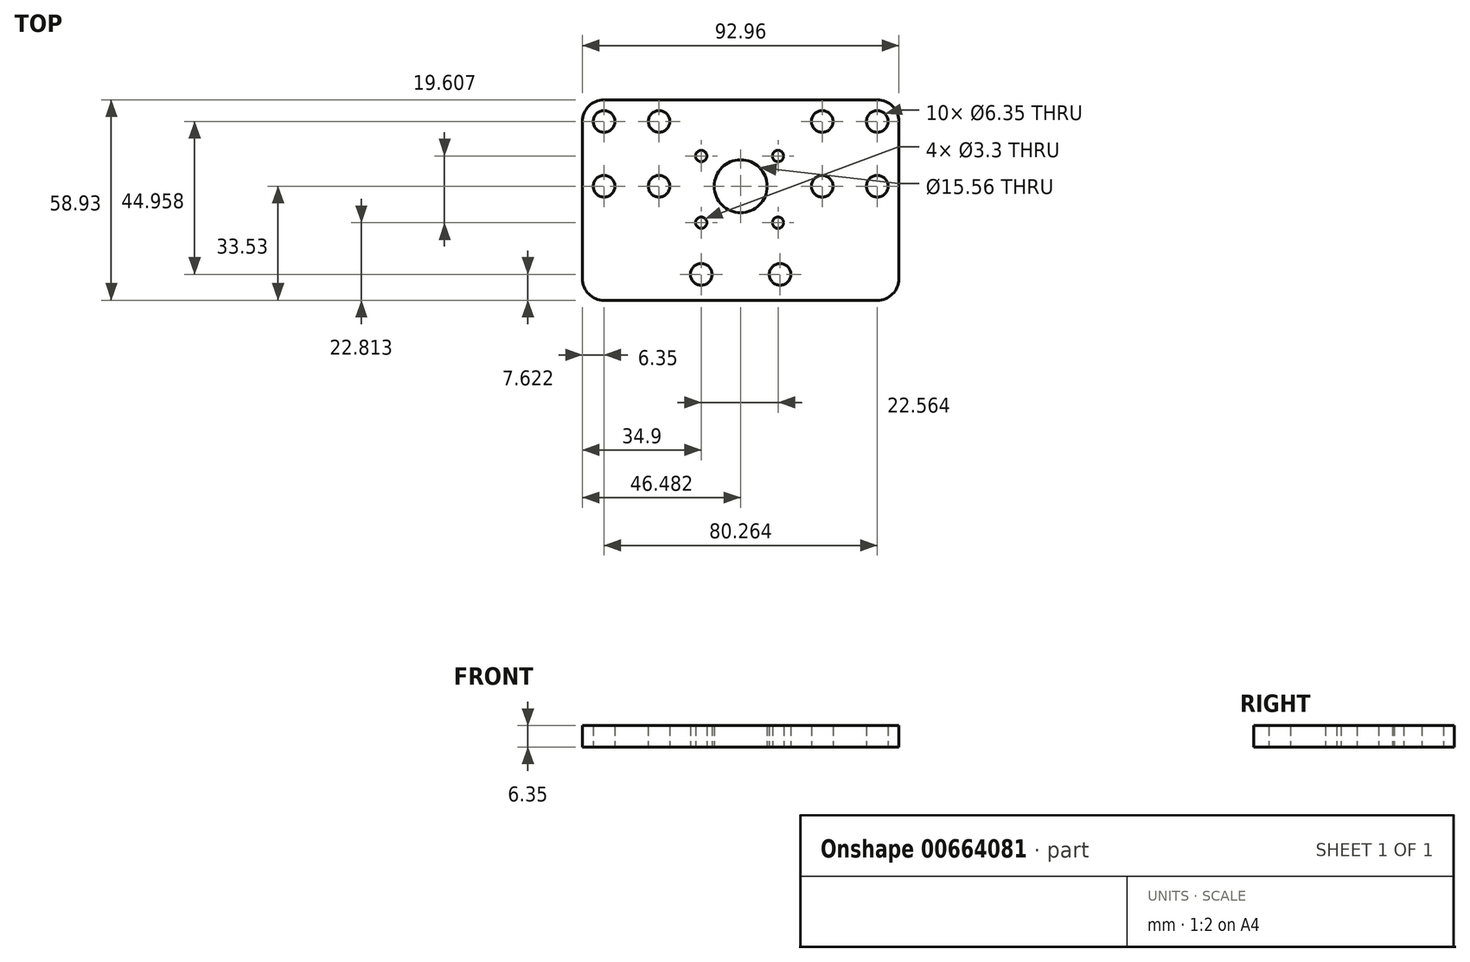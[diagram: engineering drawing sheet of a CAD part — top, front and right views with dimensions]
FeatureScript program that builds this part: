
annotation { "Feature Type Name" : "Feature", "Feature Type Description" : "" }
export const myFeature = defineFeature(function(context is Context, id is Id, definition is map)
    precondition{}
    {
        {
            var Q0;
            Q0=qCreatedBy(makeId("Top.planeOp"),FACE);
            var sketch = newSketch(context, id + "F0", { "sketchPlane" : qUnion([Q0])});
            skLineSegment(sketch, "E0.bottom", {"start": v(6.35, 0) * mm, "end": v(86.61, 0) * mm});
            skLineSegment(sketch, "E0.top", {"start": v(6.35, -58.93) * mm, "end": v(86.61, -58.93) * mm});
            skLineSegment(sketch, "E0.left", {"start": v(0, -6.35) * mm, "end": v(0, -52.58) * mm});
            skLineSegment(sketch, "E0.right", {"start": v(92.96, -6.35) * mm, "end": v(92.96, -52.58) * mm});
            skPoint(sketch, "E1.visualSharp", {"position": v(0, 0) * mm});
            skArc(sketch, "E1.filletArc", {"start": v(6.35, 0) * mm, "mid": v(1.86, -1.86) * mm, "end": v(0, -6.35) * mm});
            skPoint(sketch, "E2.visualSharp", {"position": v(0, -58.93) * mm});
            skArc(sketch, "E2.filletArc", {"start": v(0, -52.58) * mm, "mid": v(1.86, -57.07) * mm, "end": v(6.35, -58.93) * mm});
            skPoint(sketch, "E3.visualSharp", {"position": v(92.96, -58.93) * mm});
            skArc(sketch, "E3.filletArc", {"start": v(86.61, -58.93) * mm, "mid": v(91.1, -57.07) * mm, "end": v(92.96, -52.58) * mm});
            skPoint(sketch, "E4.visualSharp", {"position": v(92.96, 0) * mm});
            skArc(sketch, "E4.filletArc", {"start": v(92.96, -6.35) * mm, "mid": v(91.1, -1.86) * mm, "end": v(86.61, 0) * mm});
            skCircle(sketch, "E5", {"center": v(6.35, -6.35) * mm, "radius": 3.18 * mm});
            skCircle(sketch, "E6", {"center": v(22.53, -6.35) * mm, "radius": 3.18 * mm});
            skLineSegment(sketch, "E7", {"start": v(46.48, 0) * mm, "end": v(46.48, -15.24) * mm, "construction": true});
            skCircle(sketch, "E8", {"center": v(6.35, -25.4) * mm, "radius": 3.18 * mm});
            skCircle(sketch, "E9", {"center": v(22.52, -25.4) * mm, "radius": 3.18 * mm});
            skCircle(sketch, "E10", {"center": v(46.48, -25.4) * mm, "radius": 7.78 * mm});
            skCircle(sketch, "E11", {"center": v(34.9, -16.51) * mm, "radius": 1.65 * mm});
            skCircle(sketch, "E12", {"center": v(34.9, -36.12) * mm, "radius": 1.65 * mm});
            skCircle(sketch, "E13", {"center": v(34.9, -51.3) * mm, "radius": 3.18 * mm});
            skCircle(sketch, "E14", {"center": v(86.61, -6.35) * mm, "radius": 3.18 * mm});
            skCircle(sketch, "E15", {"center": v(70.43, -6.35) * mm, "radius": 3.18 * mm});
            skCircle(sketch, "E16", {"center": v(70.43, -25.4) * mm, "radius": 3.18 * mm});
            skCircle(sketch, "E17", {"center": v(86.61, -25.4) * mm, "radius": 3.18 * mm});
            skCircle(sketch, "E18", {"center": v(57.46, -16.51) * mm, "radius": 1.65 * mm});
            skCircle(sketch, "E19", {"center": v(57.46, -36.12) * mm, "radius": 1.65 * mm});
            skLineSegment(sketch, "E20", {"start": v(46.48, -58.93) * mm, "end": v(46.48, -49.8) * mm, "construction": true});
            skCircle(sketch, "E21", {"center": v(58.06, -51.3) * mm, "radius": 3.18 * mm});
            skLineSegment(sketch, "E22", {"start": v(57.46, -16.51) * mm, "end": v(57.46, -36.12) * mm, "construction": true});
            skLineSegment(sketch, "E23", {"start": v(34.9, -16.51) * mm, "end": v(34.9, -36.12) * mm, "construction": true});
            skLineSegment(sketch, "E24", {"start": v(57.46, -36.12) * mm, "end": v(34.9, -36.12) * mm, "construction": true});
            skSolve(sketch);
        }
        {
            var Q0;
            Q0=makeQuery(id+"F0.imprint","IMPRINT",FACE,{"disambiguationData":[TD([[makeQuery(id+"F0.imprint","IMPRINT",EDGE,{"derivedFrom":sQuery(id+"F0.wireOp",EDGE,"E0.bottom")}),-1.0]])]});
            extrude(context, id + "F1", {"entities" : qUnion([Q0]), "depth" : 6.35 * mm, "offsetDistance" : 25.4 * mm});
        }
    });
